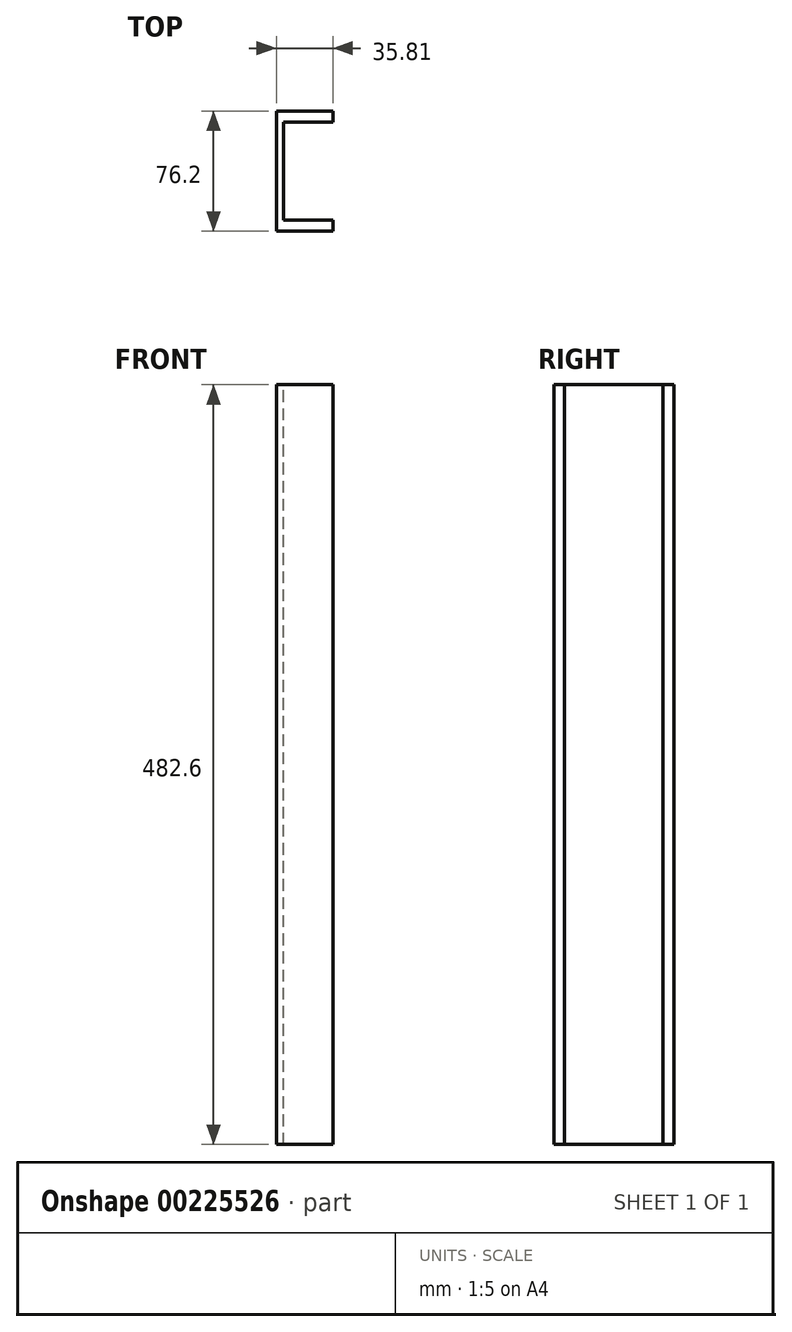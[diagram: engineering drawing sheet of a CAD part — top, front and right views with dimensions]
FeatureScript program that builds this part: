
annotation { "Feature Type Name" : "Feature", "Feature Type Description" : "" }
export const myFeature = defineFeature(function(context is Context, id is Id, definition is map)
    precondition{}
    {
        {
            var Q0;
            Q0=qCreatedBy(makeId("Right.planeOp"),FACE);
            var sketch = newSketch(context, id + "F0", { "sketchPlane" : qUnion([Q0])});
            skLineSegment(sketch, "E0.bottom", {"start": v(36.77, 268.24) * mm, "end": v(-39.43, 268.24) * mm});
            skLineSegment(sketch, "E0.top", {"start": v(36.77, -214.36) * mm, "end": v(-39.43, -214.36) * mm});
            skLineSegment(sketch, "E0.left", {"start": v(36.77, 268.24) * mm, "end": v(36.77, -214.36) * mm});
            skLineSegment(sketch, "E0.right", {"start": v(-39.43, 268.24) * mm, "end": v(-39.43, -214.36) * mm});
            skSolve(sketch);
        }
        {
            var Q0;
            Q0 = qSketchRegion(id + "F0", true);
            extrude(context, id + "F1", {"entities" : qUnion([Q0]), "depth" : 35.81 * mm});
        }
        {
            var Q0;
            Q0=makeQuery(id+"F1.opExtrude","SWEPT_FACE",FACE,{"disambiguationData":[OSD([sQuery(id+"F0.wireOp",EDGE,"E0.bottom")])]});
            var sketch = newSketch(context, id + "F2", { "sketchPlane" : qUnion([Q0])});
            skLineSegment(sketch, "E1.bottom", {"start": v(35.81, 29.84) * mm, "end": v(4.32, 29.84) * mm});
            skLineSegment(sketch, "E1.top", {"start": v(35.81, -32.5) * mm, "end": v(4.32, -32.5) * mm});
            skLineSegment(sketch, "E1.left", {"start": v(35.81, 29.84) * mm, "end": v(35.81, -32.5) * mm});
            skLineSegment(sketch, "E1.right", {"start": v(4.32, 29.84) * mm, "end": v(4.32, -32.5) * mm});
            skSolve(sketch);
        }
        {
            var Q0;
            Q0 = qSketchRegion(id + "F2", true);
            extrude(context, id + "F3", {"entities" : qUnion([Q0]), "operationType" : NewBodyOperationType.REMOVE, "endBound" : BoundingType.THROUGH_ALL, "oppositeDirection" : true, "depth" : 25.4 * mm});
        }
    });
